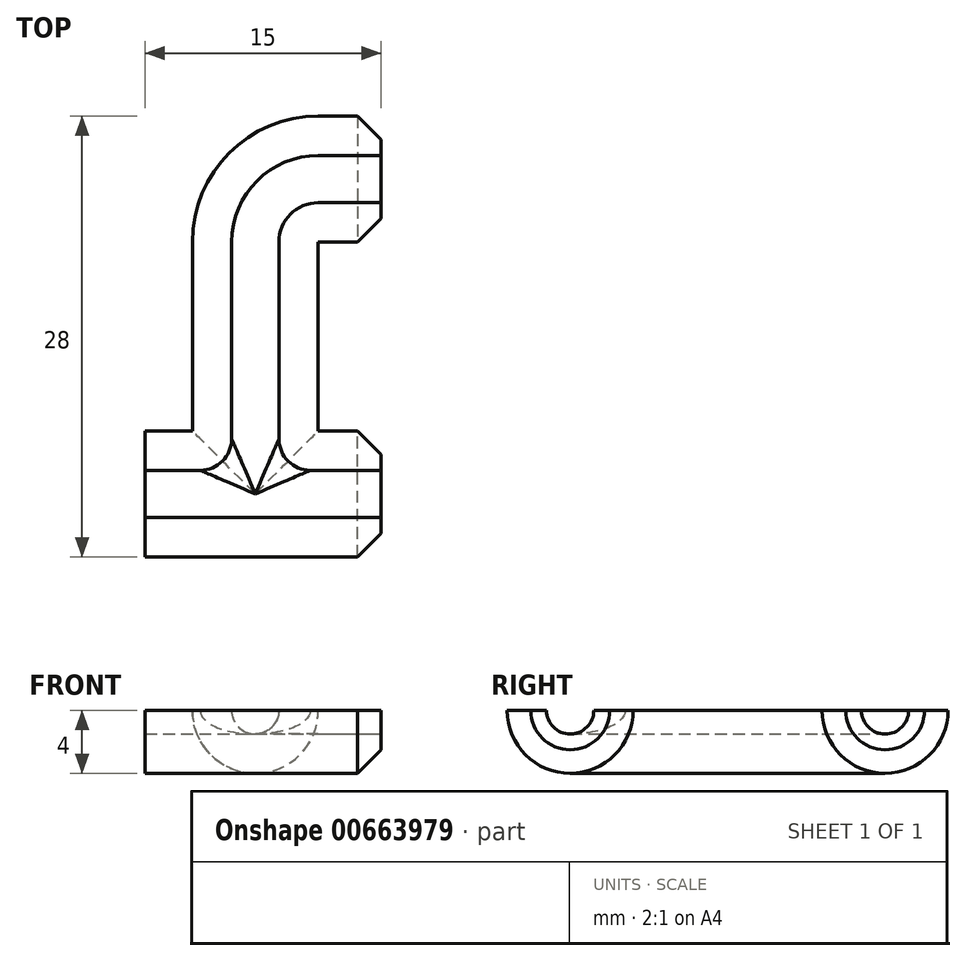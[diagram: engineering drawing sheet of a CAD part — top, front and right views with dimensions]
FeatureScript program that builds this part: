
annotation { "Feature Type Name" : "Feature", "Feature Type Description" : "" }
export const myFeature = defineFeature(function(context is Context, id is Id, definition is map)
    precondition{}
    {
        {
            var Q0;
            Q0=qCreatedBy(makeId("Top.planeOp"),FACE);
            var sketch = newSketch(context, id + "F0", { "sketchPlane" : qUnion([Q0])});
            skLineSegment(sketch, "E0", {"start": v(-7, 0) * mm, "end": v(8, 0) * mm});
            skLineSegment(sketch, "E1", {"start": v(0, 0) * mm, "end": v(0, 16) * mm});
            skLineSegment(sketch, "E2", {"start": v(4, 20) * mm, "end": v(8, 20) * mm});
            skLineSegment(sketch, "E3", {"start": v(-7, 0) * mm, "end": v(-22, 0) * mm, "construction": true});
            skLineSegment(sketch, "E4", {"start": v(8, 0) * mm, "end": v(13, 0) * mm, "construction": true});
            skLineSegment(sketch, "E5", {"start": v(8, 20) * mm, "end": v(13, 20) * mm, "construction": true});
            skPoint(sketch, "E6.visualSharp", {"position": v(0, 20) * mm});
            skArc(sketch, "E6.filletArc", {"start": v(4, 20) * mm, "mid": v(1.17, 18.83) * mm, "end": v(0, 16) * mm});
            skSolve(sketch);
        }
        {
            var Q0;
            Q0=qCreatedBy(makeId("Right.planeOp"),FACE);
            var sketch = newSketch(context, id + "F1", { "sketchPlane" : qUnion([Q0])});
            skCircle(sketch, "E7", {"center": v(0, 0) * mm, "radius": 4 * mm});
            skSolve(sketch);
        }
        {
            var Q0;
            Q0 = qSketchRegion(id + "F1", true);
            var Q1;
            Q1=sQuery(id+"F0.wireOp",EDGE,"E0");
            sweep(context, id + "F2", {"profiles" : qUnion([Q0]), "path" : qUnion([Q1])});
        }
        {
            var Q0;
            Q0=qCreatedBy(makeId("Front.planeOp"),FACE);
            var sketch = newSketch(context, id + "F3", { "sketchPlane" : qUnion([Q0])});
            skCircle(sketch, "E8", {"center": v(0, 0) * mm, "radius": 4 * mm});
            skSolve(sketch);
        }
        {
            var Q0;
            Q0 = qSketchRegion(id + "F3", true);
            var Q1;
            Q1=sQuery(id+"F0.wireOp",EDGE,"E1");
            var Q2;
            Q2=sQuery(id+"F0.wireOp",EDGE,"E6.filletArc");
            var Q3;
            Q3=sQuery(id+"F0.wireOp",EDGE,"E2");
            sweep(context, id + "F4", {"operationType" : NewBodyOperationType.ADD, "profiles" : qUnion([Q0]), "path" : qUnion([Q1, Q2, Q3])});
        }
        {
            var Q0;
            Q0=makeQuery(id+"F2.opSweep","CAP_EDGE",EDGE,{"disambiguationData":[OSD([sQuery(id+"F0.wireOp",VERTEX,"E0.end"),sQuery(id+"F1.wireOp",EDGE,"E7")])],"isStart":false});
            var Q1;
            Q1=makeQuery(id+"F4.opSweep","CAP_EDGE",EDGE,{"disambiguationData":[OSD([sQuery(id+"F0.wireOp",VERTEX,"E2.end"),sQuery(id+"F3.wireOp",EDGE,"E8")])],"isStart":false});
            chamfer(context, id + "F5", {"entities" : qUnion([Q0, Q1]), "width" : 1.5 * mm, "tangentPropagation" : true});
        }
        {
            var Q0;
            Q0=qCreatedBy(makeId("Front.planeOp"),FACE);
            var sketch = newSketch(context, id + "F6", { "sketchPlane" : qUnion([Q0])});
            skLineSegment(sketch, "E9.bottom", {"start": v(-16.1, 0) * mm, "end": v(30.16, 0) * mm});
            skLineSegment(sketch, "E9.top", {"start": v(-16.1, 7.9) * mm, "end": v(30.16, 7.9) * mm});
            skLineSegment(sketch, "E9.left", {"start": v(-16.1, 0) * mm, "end": v(-16.1, 7.9) * mm});
            skLineSegment(sketch, "E9.right", {"start": v(30.16, 0) * mm, "end": v(30.16, 7.9) * mm});
            skSolve(sketch);
        }
        {
            var Q0;
            Q0=makeQuery(id+"F6.imprint","IMPRINT",FACE,{"disambiguationData":[TD([[makeQuery(id+"F6.imprint","IMPRINT",EDGE,{"derivedFrom":sQuery(id+"F6.wireOp",EDGE,"E9.bottom")}),1.0]])]});
            extrude(context, id + "F7", {"entities" : qUnion([Q0]), "operationType" : NewBodyOperationType.REMOVE, "oppositeDirection" : true, "depth" : 25 * mm, "offsetDistance" : 25 * mm, "hasSecondDirection" : true, "secondDirectionOppositeDirection" : false, "secondDirectionDepth" : 25 * mm});
        }
        {
            var Q0;
            Q0=qCreatedBy(makeId("Right.planeOp"),FACE);
            var sketch = newSketch(context, id + "F8", { "sketchPlane" : qUnion([Q0])});
            skCircle(sketch, "E10", {"center": v(0, 0) * mm, "radius": 1.5 * mm});
            skSolve(sketch);
        }
        {
            var Q0;
            Q0 = qSketchRegion(id + "F8", true);
            var Q1;
            Q1=sQuery(id+"F0.wireOp",EDGE,"E0");
            sweep(context, id + "F9", {"operationType" : NewBodyOperationType.REMOVE, "profiles" : qUnion([Q0]), "path" : qUnion([Q1])});
        }
        {
            var Q0;
            Q0=qCreatedBy(makeId("Front.planeOp"),FACE);
            var sketch = newSketch(context, id + "F10", { "sketchPlane" : qUnion([Q0])});
            skCircle(sketch, "E11", {"center": v(0, 0) * mm, "radius": 1.5 * mm});
            skSolve(sketch);
        }
        {
            var Q0;
            Q0 = qSketchRegion(id + "F10", true);
            var Q1;
            Q1=sQuery(id+"F0.wireOp",EDGE,"E1");
            var Q2;
            Q2=sQuery(id+"F0.wireOp",EDGE,"E6.filletArc");
            var Q3;
            Q3=sQuery(id+"F0.wireOp",EDGE,"E2");
            sweep(context, id + "F11", {"operationType" : NewBodyOperationType.REMOVE, "profiles" : qUnion([Q0]), "path" : qUnion([Q1, Q2, Q3])});
        }
        {
            var Q0;
            Q0=qCreatedBy(makeId("Front.planeOp"),FACE);
            var sketch = newSketch(context, id + "F12", { "sketchPlane" : qUnion([Q0])});
            skCircle(sketch, "E12", {"center": v(-14.07, 0) * mm, "radius": 7.5 * mm});
            skSolve(sketch);
        }
        {
            var Q0;
            Q0=makeQuery(id+"F11.boolean.opBoolean","COPY",EDGE,{"derivedFrom":makeQuery(id+"F11.opSweep","MID_CAP_EDGE",EDGE,{"disambiguationData":[OSD([sQuery(id+"F0.wireOp",VERTEX,"E2.start"),sQuery(id+"F10.wireOp",EDGE,"E11")])],"capPos":1.0})});
            var Q1;
            Q1=makeQuery(id+"F11.boolean.opBoolean","INTERSECT",EDGE,{"disambiguationData":[OD(0.0)],"derivedFrom":[makeQuery(id+"F9.boolean.opBoolean","COPY",FACE,{"derivedFrom":makeQuery(id+"F9.opSweep","SWEPT_FACE",FACE,{"disambiguationData":[OSD([sQuery(id+"F0.wireOp",EDGE,"E0"),sQuery(id+"F8.wireOp",EDGE,"E10")])]})}),makeQuery(id+"F11.opSweep","SWEPT_FACE",FACE,{"disambiguationData":[OSD([sQuery(id+"F0.wireOp",EDGE,"E1"),sQuery(id+"F10.wireOp",EDGE,"E11")])]})]});
            var Q2;
            Q2=makeQuery(id+"F11.boolean.opBoolean","INTERSECT",EDGE,{"disambiguationData":[OD(1.0)],"derivedFrom":[makeQuery(id+"F9.boolean.opBoolean","COPY",FACE,{"derivedFrom":makeQuery(id+"F9.opSweep","SWEPT_FACE",FACE,{"disambiguationData":[OSD([sQuery(id+"F0.wireOp",EDGE,"E0"),sQuery(id+"F8.wireOp",EDGE,"E10")])]})}),makeQuery(id+"F11.opSweep","SWEPT_FACE",FACE,{"disambiguationData":[OSD([sQuery(id+"F0.wireOp",EDGE,"E1"),sQuery(id+"F10.wireOp",EDGE,"E11")])]})]});
            fillet(context, id + "F13", {"entities" : qUnion([Q0, Q1, Q2]), "radius" : 2 * mm, "tangentPropagation" : true, "allowEdgeOverflow" : false});
        }
    });
